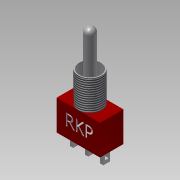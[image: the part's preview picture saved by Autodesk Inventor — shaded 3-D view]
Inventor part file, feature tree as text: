
AUTODESK INVENTOR PART (.ipt)
format: ipt  version: 2015 SP1 (Build 190203100, 203)  size: 288,768 bytes
history: native  units: mm
features: extrude x6, sketch x6, thread x1, shell x1, fillet x1, projected_geometry x1
ambient origin geometry x8: Origin, YZ Plane, XZ Plane, XY Plane, X Axis, Y Axis, Z Axis, Center Point
bodies: Solid1 (feature_tree)
feature tree (16):
  extrude  "Extrusion1"  Depth=7.0mm
  extrude  "Extrusion2"  Depth=9.0mm
  thread  "Thread1"  [1 undecoded]
  extrude  "Extrusion3"  Depth=10.0mm
  extrude  "Extrusion4"  Depth=20.0mm
  shell  "Shell1"  Thickness=4.0mm
  extrude  "Extrusion5"  Depth=2.0mm
  fillet  "Fillet1"  Radius=0.25mm
  extrude  "Extrusion6"  Depth=1.5mm
  sketch  "Sketch1"  dims[d0=13.0mm d1=7.0mm]
  sketch  "Sketch2"  dims[d2=9.0mm d3=0.0mm d4=7.0mm d5=9.0mm d6=0.0mm]
  sketch  "Sketch3"  dims[d7=10.0mm d8=0.0mm d9=1.0mm]
  sketch  "Sketch4"  dims[d10=2.0mm d11=20.0mm d13=4.5mm d14=20.0mm d16=4.5mm d19=4.0mm d20=0.0mm]
  projected_geometry  "Projected Loop1"
  sketch  "Sketch5"  dims[d21=1.0mm d22=2.0mm d23=0.25mm]
  sketch  "Sketch6"  dims[d24=4.0mm d25=0.0mm d26=0.3mm d27=3.0mm d28=20.0mm d29=0.0mm d30=1.5mm d31=3.4mm d32=0.0mm]
note: 1 required parameter value undecoded (feature->parameter linkage not recoverable at this tier; creation-order binding heuristic only, values carry confidence <= 0.55)
